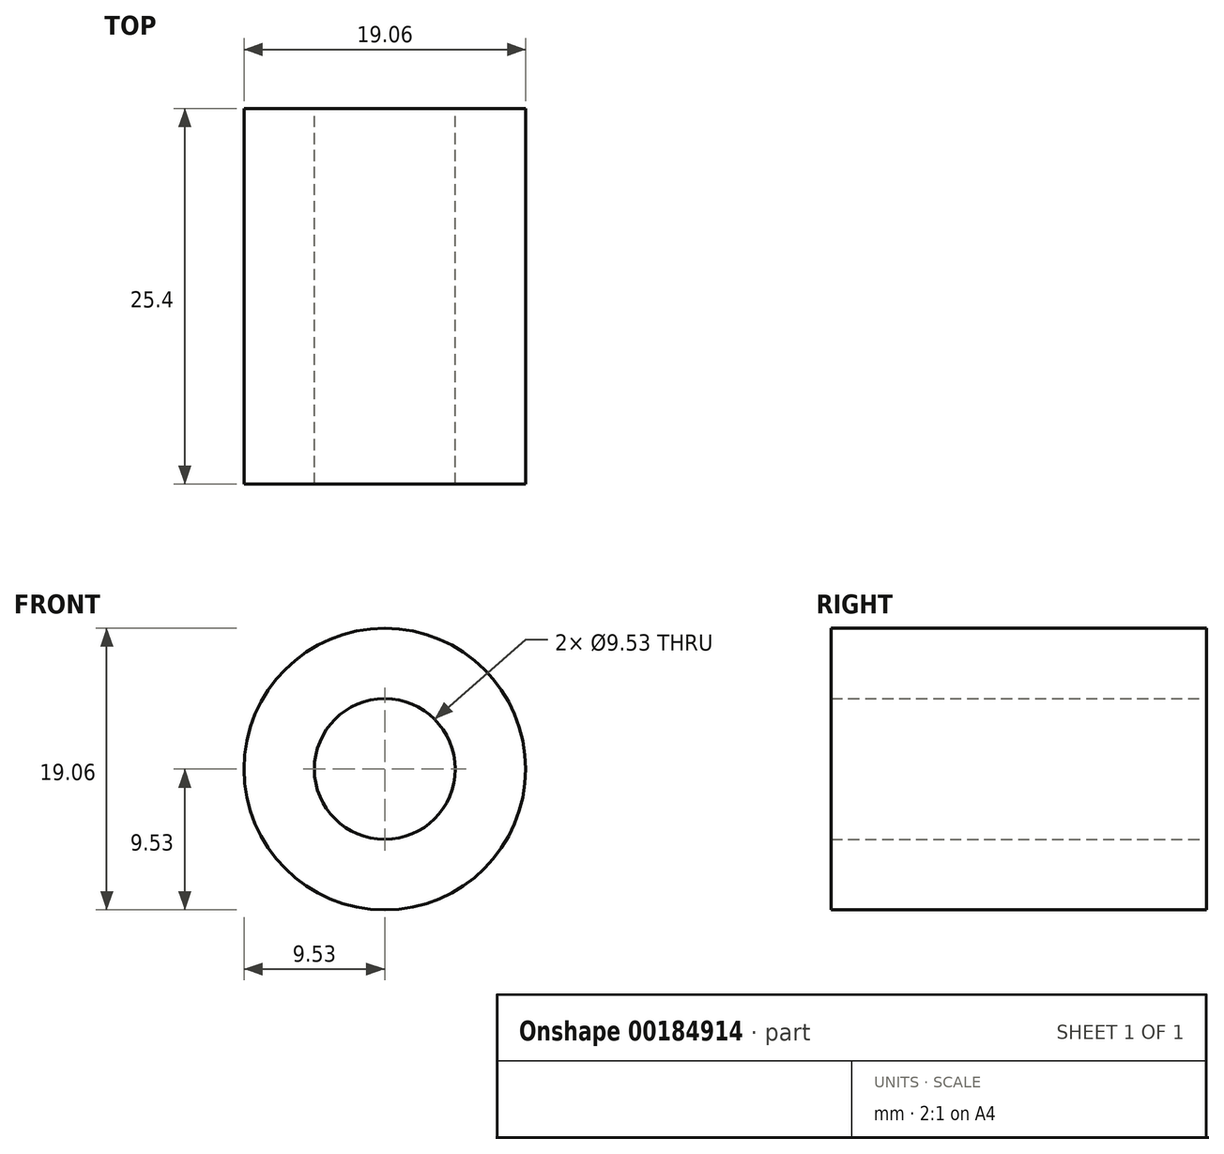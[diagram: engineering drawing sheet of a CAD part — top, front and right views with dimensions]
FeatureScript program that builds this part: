
annotation { "Feature Type Name" : "Feature", "Feature Type Description" : "" }
export const myFeature = defineFeature(function(context is Context, id is Id, definition is map)
    precondition{}
    {
        {
            var Q0;
            Q0=qCreatedBy(makeId("Front.planeOp"),FACE);
            var sketch = newSketch(context, id + "F0", { "sketchPlane" : qUnion([Q0])});
            skCircle(sketch, "E0", {"center": v(0, 0) * mm, "radius": 9.53 * mm});
            skSolve(sketch);
        }
        {
            var Q0;
            Q0 = qSketchRegion(id + "F0", true);
            extrude(context, id + "F1", {"entities" : qUnion([Q0]), "depth" : 25.4 * mm});
        }
        {
            var Q0;
            Q0=qCreatedBy(makeId("Front.planeOp"),FACE);
            var sketch = newSketch(context, id + "F2", { "sketchPlane" : qUnion([Q0])});
            skLineSegment(sketch, "E1.bottom", {"start": v(4.76, 4.76) * mm, "end": v(-4.76, 4.76) * mm});
            skLineSegment(sketch, "E1.top", {"start": v(4.76, -4.76) * mm, "end": v(-4.76, -4.76) * mm});
            skLineSegment(sketch, "E1.left", {"start": v(4.76, 4.76) * mm, "end": v(4.76, -4.76) * mm});
            skLineSegment(sketch, "E1.right", {"start": v(-4.76, 4.76) * mm, "end": v(-4.76, -4.76) * mm});
            skPoint(sketch, "E1.middle", {"position": v(0, 0) * mm});
            skCircle(sketch, "E2", {"center": v(0, 0) * mm, "radius": 4.76 * mm});
            skSolve(sketch);
        }
        {
            var Q0;
            {var subQ0=sQuery(id+"F2.wireOp",EDGE,"E2");var subQ1=makeQuery(id+"F2.imprint","INTERSECT",VERTEX,{"derivedFrom":[sQuery(id+"F2.wireOp",EDGE,"E1.bottom"),subQ0]});Q0=makeQuery(id+"F2.imprint","IMPRINT",FACE,{"disambiguationData":[TD([[makeQuery(id+"F2.imprint","IMPRINT",EDGE,{"disambiguationData":[TD([[subQ1,1.0]])],"derivedFrom":subQ0}),1.0]])]});}
            var Q1;
            Q1=sQuery(id+"F2.wireOp",EDGE,"E2");
            extrude(context, id + "F3", {"entities" : qUnion([Q0]), "operationType" : NewBodyOperationType.REMOVE, "surfaceEntities" : qUnion([Q1]), "endBound" : BoundingType.THROUGH_ALL, "depth" : 25.4 * mm});
        }
    });
